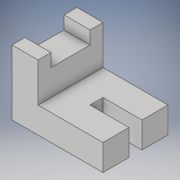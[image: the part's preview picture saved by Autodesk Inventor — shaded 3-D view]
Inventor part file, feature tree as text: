
AUTODESK INVENTOR PART (.ipt)
format: ipt  version: 2018 (Build 220112000, 112)  size: 124,928 bytes
history: native  units: in
note: dims shown in document units (in); Inventor stores cm internally (conversion verified against a paired STEP export)
features: extrude x3, sketch x3
ambient origin geometry x8: Origin, YZ Plane, XZ Plane, XY Plane, X Axis, Y Axis, Z Axis, Center Point
bodies: Solid1 (feature_tree)
feature tree (6):
  extrude  "Extrusion1"  Depth=1.25in
  extrude  "Extrusion2"  Depth=0.5in
  extrude  "Extrusion3"  Depth=1.25in TaperAngle=0.0deg
  sketch  "Sketch1"  dims[d0=0.5in d1=1.25in]
  sketch  "Sketch2"  dims[d4=1.25in d5=0.5in]
  sketch  "Sketch3"  dims[d6=0.5in d7=1.25in d8=0.0in d11=0.625in d13=0.25in d14=0.125in d15=0.75in d16=0.0in d17=1.75in d18=0.25in d19=0.25in d20=0.25in d21=0.75in d22=0.0in]
